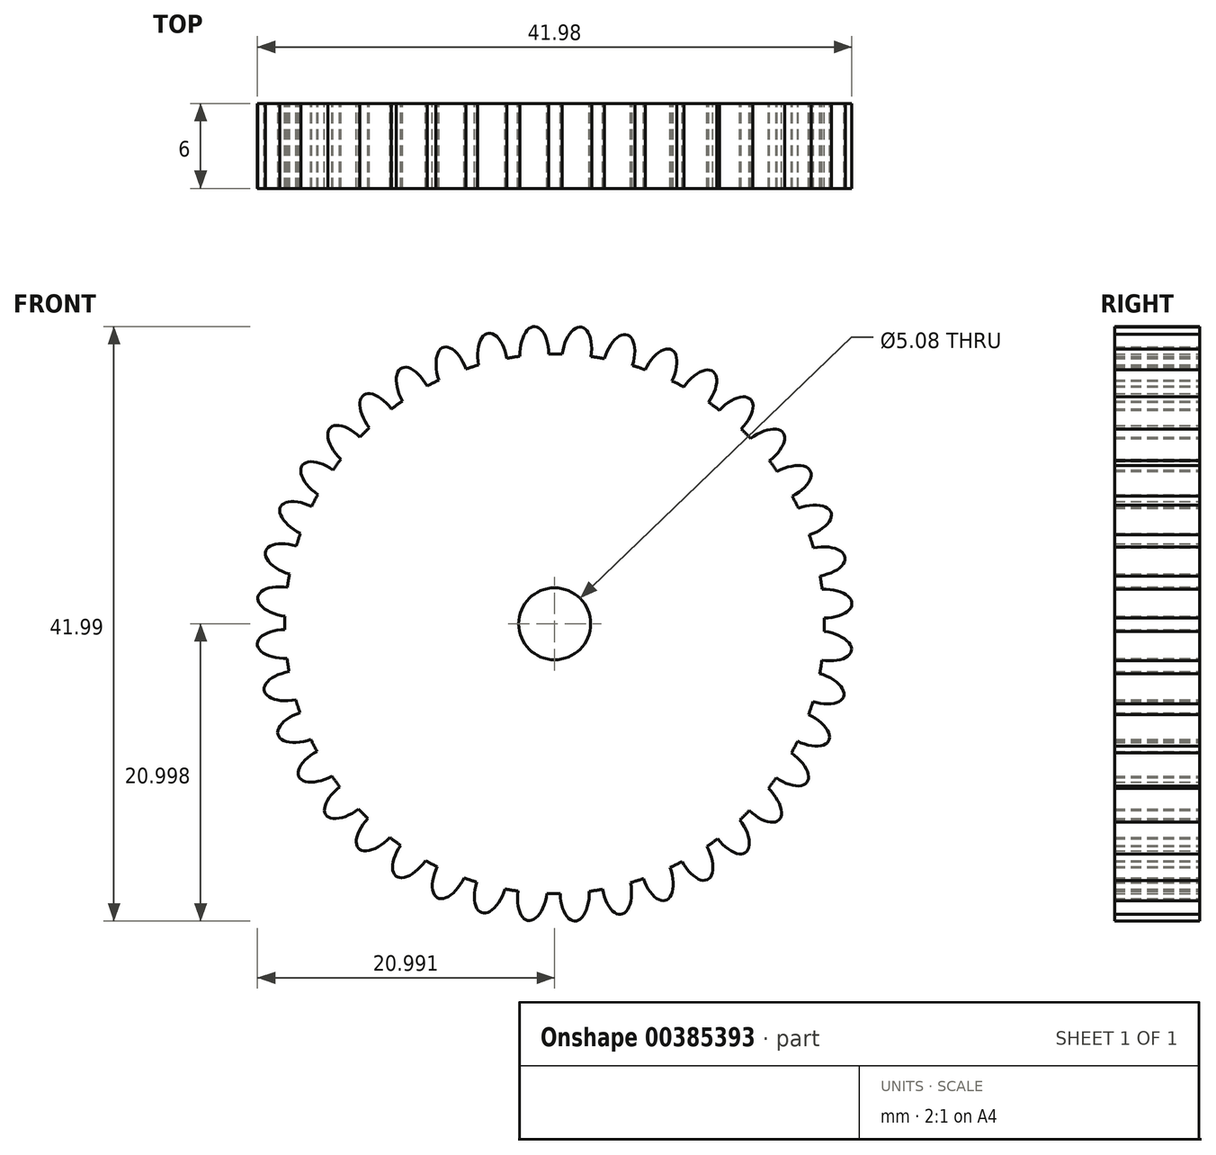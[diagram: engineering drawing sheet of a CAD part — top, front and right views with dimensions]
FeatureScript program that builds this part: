
annotation { "Feature Type Name" : "Feature", "Feature Type Description" : "" }
export const myFeature = defineFeature(function(context is Context, id is Id, definition is map)
    precondition{}
    {
        {
            var Q0;
            Q0=qCreatedBy(makeId("Front.planeOp"),FACE);
            var sketch = newSketch(context, id + "F0", { "sketchPlane" : qUnion([Q0])});
            skCircle(sketch, "E0", {"center": v(0.02, -0.42) * mm, "radius": 19.05 * mm});
            skLineSegment(sketch, "E1", {"start": v(0.02, -0.42) * mm, "end": v(-2.42, 18.47) * mm});
            skLineSegment(sketch, "E2", {"start": v(0.02, -0.42) * mm, "end": v(0.56, 18.62) * mm});
            skEllipticalArc(sketch, "E3", {});
            skEllipticalArc(sketch, "E4.1.0", {});
            skEllipticalArc(sketch, "E4.2.0", {});
            skEllipticalArc(sketch, "E4.3.0", {});
            skEllipticalArc(sketch, "E4.4.0", {});
            skEllipticalArc(sketch, "E4.5.0", {});
            skEllipticalArc(sketch, "E4.6.0", {});
            skEllipticalArc(sketch, "E4.7.0", {});
            skEllipticalArc(sketch, "E4.8.0", {});
            skEllipticalArc(sketch, "E4.9.0", {});
            skEllipticalArc(sketch, "E4.10.0", {});
            skEllipticalArc(sketch, "E4.11.0", {});
            skEllipticalArc(sketch, "E4.12.0", {});
            skEllipticalArc(sketch, "E4.13.0", {});
            skEllipticalArc(sketch, "E4.14.0", {});
            skEllipticalArc(sketch, "E4.15.0", {});
            skEllipticalArc(sketch, "E4.16.0", {});
            skEllipticalArc(sketch, "E4.17.0", {});
            skEllipticalArc(sketch, "E4.18.0", {});
            skEllipticalArc(sketch, "E4.19.0", {});
            skEllipticalArc(sketch, "E4.20.0", {});
            skEllipticalArc(sketch, "E4.21.0", {});
            skEllipticalArc(sketch, "E4.22.0", {});
            skEllipticalArc(sketch, "E4.23.0", {});
            skEllipticalArc(sketch, "E4.24.0", {});
            skEllipticalArc(sketch, "E4.25.0", {});
            skEllipticalArc(sketch, "E4.26.0", {});
            skEllipticalArc(sketch, "E4.27.0", {});
            skEllipticalArc(sketch, "E4.28.0", {});
            skEllipticalArc(sketch, "E4.29.0", {});
            skEllipticalArc(sketch, "E4.30.0", {});
            skEllipticalArc(sketch, "E4.31.0", {});
            skEllipticalArc(sketch, "E4.32.0", {});
            skEllipticalArc(sketch, "E4.33.0", {});
            skEllipticalArc(sketch, "E4.34.0", {});
            skEllipticalArc(sketch, "E4.35.0", {});
            skEllipticalArc(sketch, "E4.36.0", {});
            skEllipticalArc(sketch, "E4.37.0", {});
            skEllipticalArc(sketch, "E4.38.0", {});
            skEllipticalArc(sketch, "E4.39.0", {});
            skCircle(sketch, "E5", {"center": v(0.02, -0.42) * mm, "radius": 2.54 * mm});
            const initialGuessF0  = {"E3": [-0.0014052475357174167, 0.018575024339191597, 0, -1, 0.0019970374462838095, 0.001020793009534155, 1.595411977370606, 4.764581646804509], "E4.1.0": [-0.004359396440337886, 0.018118003329088386, 0.15643446504023098, -0.9876883405951378, 0.0019970374462838095, 0.001020793009534155, 1.595411977370606, 4.764581646804509], "E4.2.0": [-0.007205681032585775, 0.01720447830245893, 0.3090169943749475, -0.9510565162951535, 0.0019970374462838095, 0.001020793009534155, 1.595411977370606, 4.764581646804509], "E4.3.0": [-0.00987401633952296, 0.01585694327727463, 0.45399049973954686, -0.8910065241883678, 0.0019970374462838095, 0.001020793009534155, 1.595411977370606, 4.764581646804509], "E4.4.0": [-0.012298699090195491, 0.014108579038067826, 0.5877852522924732, -0.8090169943749473, 0.0019970374462838095, 0.001020793009534155, 1.595411977370606, 4.764581646804509], "E4.5.0": [-0.014420025548221109, 0.012002436114896046, 0.7071067811865476, -0.7071067811865475, 0.0019970374462838095, 0.001020793009534155, 1.595411977370606, 4.764581646804509], "E4.6.0": [-0.01618576161592434, 0.009590374736415393, 0.8090169943749476, -0.587785252292473, 0.0019970374462838095, 0.001020793009534155, 1.595411977370606, 4.764581646804509], "E4.7.0": [-0.01755242901117631, 0.006931787858936823, 0.8910065241883679, -0.4539904997395467, 0.0019970374462838095, 0.001020793009534155, 1.595411977370606, 4.764581646804509], "E4.8.0": [-0.01848637584699686, 0.004092138714727838, 0.9510565162951538, -0.3090169943749474, 0.0019970374462838095, 0.001020793009534155, 1.595411977370606, 4.764581646804509], "E4.9.0": [-0.01896460525269627, 0.0011413488899740531, 0.9876883405951378, -0.1564344650402308, 0.0019970374462838095, 0.001020793009534155, 1.595411977370606, 4.764581646804509], "E4.10.0": [-0.018975341633153807, -0.0018479233767291214, 1, 0, 0.0019970374462838095, 0.001020793009534155, 1.595411977370606, 4.764581646804509], "E4.11.0": [-0.018518320623050588, -0.004802072281349587, 0.9876883405951378, 0.1564344650402307, 0.0019970374462838095, 0.001020793009534155, 1.595411977370606, 4.764581646804509], "E4.12.0": [-0.017604795596421148, -0.007648356873597481, 0.9510565162951536, 0.30901699437494745, 0.0019970374462838095, 0.001020793009534155, 1.595411977370606, 4.764581646804509], "E4.13.0": [-0.016257260571236838, -0.01031669218053467, 0.891006524188368, 0.4539904997395469, 0.0019970374462838095, 0.001020793009534155, 1.595411977370606, 4.764581646804509], "E4.14.0": [-0.014508896332030034, -0.012741374931207191, 0.8090169943749476, 0.5877852522924732, 0.001997037446283809, 0.0010207930095341548, 1.595411977370606, 4.764581646804509], "E4.15.0": [-0.012402753408858254, -0.014862701389232815, 0.7071067811865475, 0.7071067811865476, 0.0019970374462838095, 0.001020793009534155, 1.595411977370606, 4.764581646804509], "E4.16.0": [-0.009990692030377604, -0.016628437456936044, 0.5877852522924731, 0.8090169943749475, 0.0019970374462838095, 0.001020793009534155, 1.595411977370606, 4.764581646804509], "E4.17.0": [-0.0073321051528990305, -0.017995104852188016, 0.45399049973954675, 0.8910065241883679, 0.0019970374462838095, 0.001020793009534155, 1.595411977370606, 4.764581646804509], "E4.18.0": [-0.004492456008690044, -0.018929051688008566, 0.30901699437494745, 0.9510565162951538, 0.0019970374462838095, 0.001020793009534155, 1.595411977370606, 4.764581646804509], "E4.19.0": [-0.0015416661839362591, -0.01940728109370798, 0.1564344650402309, 0.9876883405951379, 0.0019970374462838095, 0.001020793009534155, 1.595411977370606, 4.764581646804509], "E4.20.0": [0.001447606082766912, -0.01941801747416551, 0, 1, 0.0019970374462838095, 0.001020793009534155, 1.595411977370606, 4.764581646804509], "E4.21.0": [0.004401754987387379, -0.018960996464062296, -0.15643446504023084, 0.9876883405951378, 0.0019970374462838095, 0.001020793009534155, 1.595411977370606, 4.764581646804509], "E4.22.0": [0.007248039579635266, -0.018047471437432863, -0.309016994374947, 0.9510565162951538, 0.0019970374462838095, 0.001020793009534155, 1.595411977370606, 4.764581646804509], "E4.23.0": [0.009916374886572462, -0.016699936412248543, -0.4539904997395469, 0.891006524188368, 0.0019970374462838095, 0.001020793009534155, 1.595411977370606, 4.764581646804509], "E4.24.0": [0.012341057637244987, -0.01495157217304174, -0.5877852522924731, 0.8090169943749475, 0.0019970374462838095, 0.001020793009534155, 1.595411977370606, 4.764581646804509], "E4.25.0": [0.014462384095270604, -0.012845429249869963, -0.7071067811865476, 0.7071067811865476, 0.0019970374462838095, 0.001020793009534155, 1.595411977370606, 4.764581646804509], "E4.26.0": [0.016228120162973834, -0.01043336787138931, -0.8090169943749475, 0.5877852522924731, 0.0019970374462838095, 0.001020793009534155, 1.595411977370606, 4.764581646804509], "E4.27.0": [0.017594787558225806, -0.007774780993910739, -0.8910065241883679, 0.4539904997395468, 0.0019970374462838095, 0.001020793009534155, 1.595411977370606, 4.764581646804509], "E4.28.0": [0.01852873439404637, -0.0049351318497017505, -0.9510565162951538, 0.3090169943749475, 0.0019970374462838095, 0.001020793009534155, 1.595411977370606, 4.764581646804509], "E4.29.0": [0.019006963799745778, -0.0019843420249479674, -0.9876883405951379, 0.15643446504023095, 0.001997037446283809, 0.0010207930095341548, 1.595411977370606, 4.764581646804509], "E4.30.0": [0.019017700180203302, 0.0010049302417552038, -1, 0, 0.0019970374462838095, 0.001020793009534155, 1.595411977370606, 4.764581646804509], "E4.31.0": [0.01856067917010009, 0.003959079146375673, -0.9876883405951378, -0.15643446504023079, 0.0019970374462838095, 0.001020793009534155, 1.595411977370606, 4.764581646804509], "E4.32.0": [0.01764715414347065, 0.006805363738623563, -0.9510565162951536, -0.30901699437494734, 0.0019970374462838095, 0.001020793009534155, 1.595411977370606, 4.764581646804509], "E4.33.0": [0.016299619118286333, 0.009473699045560755, -0.891006524188368, -0.45399049973954686, 0.0019970374462838095, 0.001020793009534155, 1.595411977370606, 4.764581646804509], "E4.34.0": [0.014551254879079533, 0.011898381796233277, -0.8090169943749477, -0.5877852522924731, 0.0019970374462838095, 0.001020793009534155, 1.595411977370606, 4.764581646804509], "E4.35.0": [0.012445111955907756, 0.014019708254258894, -0.7071067811865476, -0.7071067811865475, 0.0019970374462838095, 0.001020793009534155, 1.595411977370606, 4.764581646804509], "E4.36.0": [0.010033050577427104, 0.01578544432196213, -0.5877852522924732, -0.8090169943749475, 0.0019970374462838095, 0.001020793009534155, 1.595411977370606, 4.764581646804509], "E4.37.0": [0.007374463699948533, 0.017152111717214102, -0.45399049973954686, -0.8910065241883679, 0.0019970374462838095, 0.001020793009534155, 1.595411977370606, 4.764581646804509], "E4.38.0": [0.0045348145557395445, 0.01808605855303466, -0.3090169943749475, -0.9510565162951535, 0.0019970374462838095, 0.001020793009534155, 1.595411977370606, 4.764581646804509], "E4.39.0": [0.0015840247309857614, 0.018564287958734067, -0.156434465040231, -0.9876883405951379, 0.0019970374462838095, 0.001020793009534155, 1.595411977370606, 4.764581646804509]};
            skSetInitialGuess(sketch, initialGuessF0);
            skSolve(sketch);
        }
        {
            var Q0;
            Q0 = qSketchRegion(id + "F0", true);
            extrude(context, id + "F1", {"entities" : qUnion([Q0]), "depth" : 6 * mm});
        }
    });
